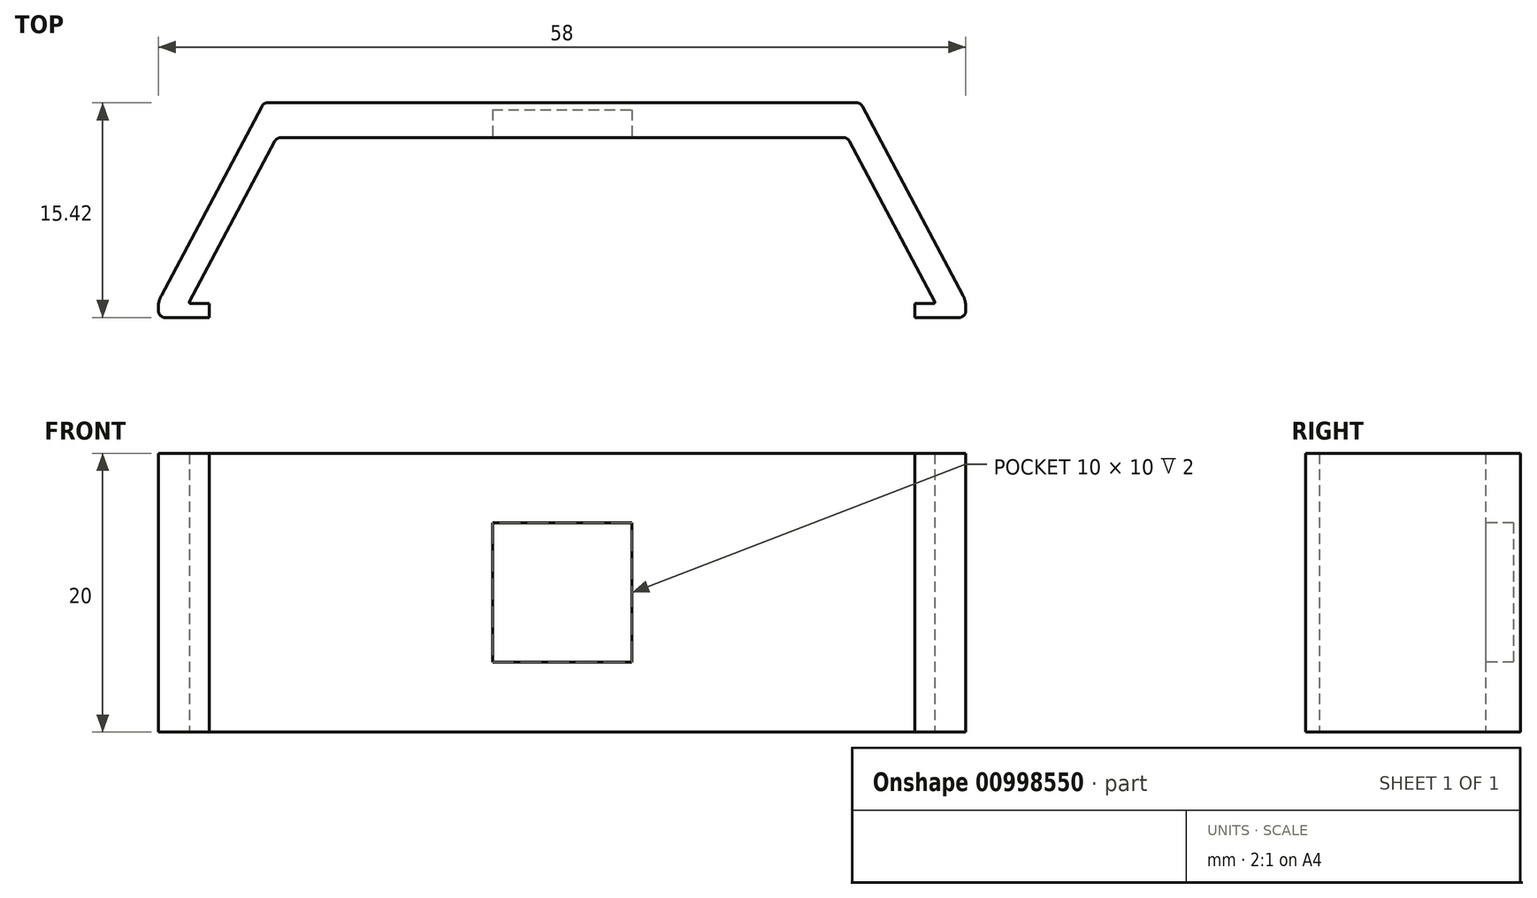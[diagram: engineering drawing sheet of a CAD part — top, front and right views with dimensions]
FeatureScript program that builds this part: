
annotation { "Feature Type Name" : "Feature", "Feature Type Description" : "" }
export const myFeature = defineFeature(function(context is Context, id is Id, definition is map)
    precondition{}
    {
        {
            var Q0;
            Q0=qCreatedBy(makeId("Top.planeOp"),FACE);
            var sketch = newSketch(context, id + "F0", { "sketchPlane" : qUnion([Q0])});
            skLineSegment(sketch, "E0", {"start": v(0, 15.42) * mm, "end": v(21.14, 15.42) * mm});
            skLineSegment(sketch, "E1", {"start": v(21.58, 15.15) * mm, "end": v(28.79, 1.6) * mm});
            skLineSegment(sketch, "E2", {"start": v(29, 0.75) * mm, "end": v(29, 0.5) * mm});
            skLineSegment(sketch, "E3", {"start": v(26.76, 1.15) * mm, "end": v(20.64, 12.65) * mm});
            skLineSegment(sketch, "E4", {"start": v(20.2, 12.92) * mm, "end": v(0, 12.92) * mm});
            skLineSegment(sketch, "E5", {"start": v(25.34, 1) * mm, "end": v(26.67, 1) * mm});
            skPoint(sketch, "E6.visualSharp", {"position": v(21.44, 15.42) * mm});
            skArc(sketch, "E6.filletArc", {"start": v(21.58, 15.15) * mm, "mid": v(21.4, 15.35) * mm, "end": v(21.14, 15.42) * mm});
            skPoint(sketch, "E7.visualSharp", {"position": v(20.5, 12.92) * mm});
            skArc(sketch, "E7.filletArc", {"start": v(20.64, 12.65) * mm, "mid": v(20.46, 12.85) * mm, "end": v(20.2, 12.92) * mm});
            skPoint(sketch, "E8.visualSharp", {"position": v(29, 1.2) * mm});
            skArc(sketch, "E8.filletArc", {"start": v(29, 0.75) * mm, "mid": v(28.94, 1.19) * mm, "end": v(28.79, 1.6) * mm});
            skPoint(sketch, "E9.visualSharp", {"position": v(29, 0) * mm});
            skArc(sketch, "E9.filletArc", {"start": v(28.5, 0) * mm, "mid": v(28.85, 0.15) * mm, "end": v(29, 0.5) * mm});
            skLineSegment(sketch, "E10", {"start": v(0, 15.42) * mm, "end": v(0, 12.92) * mm});
            skPoint(sketch, "E11.visualSharp", {"position": v(26.84, 1) * mm});
            skArc(sketch, "E12.filletArc", {"start": v(26.67, 1) * mm, "mid": v(26.76, 1.05) * mm, "end": v(26.76, 1.15) * mm});
            skLineSegment(sketch, "E13", {"start": v(25.34, 0) * mm, "end": v(28.5, 0) * mm});
            skLineSegment(sketch, "E14", {"start": v(25.34, 0) * mm, "end": v(25.34, 1) * mm});
            skSolve(sketch);
        }
        {
            var Q0;
            Q0 = qSketchRegion(id + "F0", true);
            extrude(context, id + "F1", {"entities" : qUnion([Q0]), "depth" : 20 * mm, "offsetDistance" : 25 * mm, "symmetric" : true});
        }
        {
            var Q0;
            {var subQ0=makeQuery(id+"F1.opExtrude","SWEPT_FACE",FACE,{"disambiguationData":[OSD([sQuery(id+"F0.wireOp",EDGE,"E4")])]});Q0=makeQuery(id+"F4.boolean.opBoolean","MERGE",FACE,{"derivedFrom":[subQ0,makeQuery(id+"F4.opPattern","COPY",FACE,{"derivedFrom":subQ0,"instanceName":"1"})]});}
            var sketch = newSketch(context, id + "F2", { "sketchPlane" : qUnion([Q0])});
            skLineSegment(sketch, "E15.bottom", {"start": v(0, 5) * mm, "end": v(5, 5) * mm});
            skLineSegment(sketch, "E15.top", {"start": v(0, -5) * mm, "end": v(5, -5) * mm});
            skLineSegment(sketch, "E15.left", {"start": v(0, 5) * mm, "end": v(0, -5) * mm});
            skLineSegment(sketch, "E15.right", {"start": v(5, 5) * mm, "end": v(5, -5) * mm});
            skSolve(sketch);
        }
        {
            var Q0;
            Q0=makeQuery(id+"F2.imprint","IMPRINT",FACE,{"disambiguationData":[TD([[makeQuery(id+"F2.imprint","IMPRINT",EDGE,{"derivedFrom":sQuery(id+"F2.wireOp",EDGE,"E15.bottom")}),-1.0]])]});
            extrude(context, id + "F3", {"entities" : qUnion([Q0]), "operationType" : NewBodyOperationType.REMOVE, "oppositeDirection" : true, "depth" : 2 * mm, "offsetDistance" : 25 * mm});
        }
        {
            var Q0;
            Q0=makeQuery(id+"F1.opExtrude","SWEPT_BODY",BODY,{"disambiguationData":[OSD([sQuery(id+"F0.wireOp",EDGE,"E0"),sQuery(id+"F0.wireOp",EDGE,"E1"),sQuery(id+"F0.wireOp",EDGE,"E2"),sQuery(id+"F0.wireOp",EDGE,"E3"),sQuery(id+"F0.wireOp",EDGE,"E4"),sQuery(id+"F0.wireOp",EDGE,"E5"),sQuery(id+"F0.wireOp",EDGE,"8IfDLV1I-BeuE-YOBN-EZDf-W7MQDHKdBpH4"),sQuery(id+"F0.wireOp",EDGE,"0f4VEKWE-ANGH-JvET-8YOS-xqbP80hNSniV"),sQuery(id+"F0.wireOp",EDGE,"E6.filletArc"),sQuery(id+"F0.wireOp",EDGE,"E7.filletArc"),sQuery(id+"F0.wireOp",EDGE,"E8.filletArc"),sQuery(id+"F0.wireOp",EDGE,"E9.filletArc"),sQuery(id+"F0.wireOp",EDGE,"234eca4b-4d7c-40df-88af-329d99c33e34.filletArc"),sQuery(id+"F0.wireOp",EDGE,"E10")])]});
            var Q1;
            Q1=qCreatedBy(makeId("Right.planeOp"),FACE);
            mirror(context, id + "F4", {"operationType" : NewBodyOperationType.ADD, "entities" : qUnion([Q0]), "mirrorPlane" : qUnion([Q1])});
        }
    });
